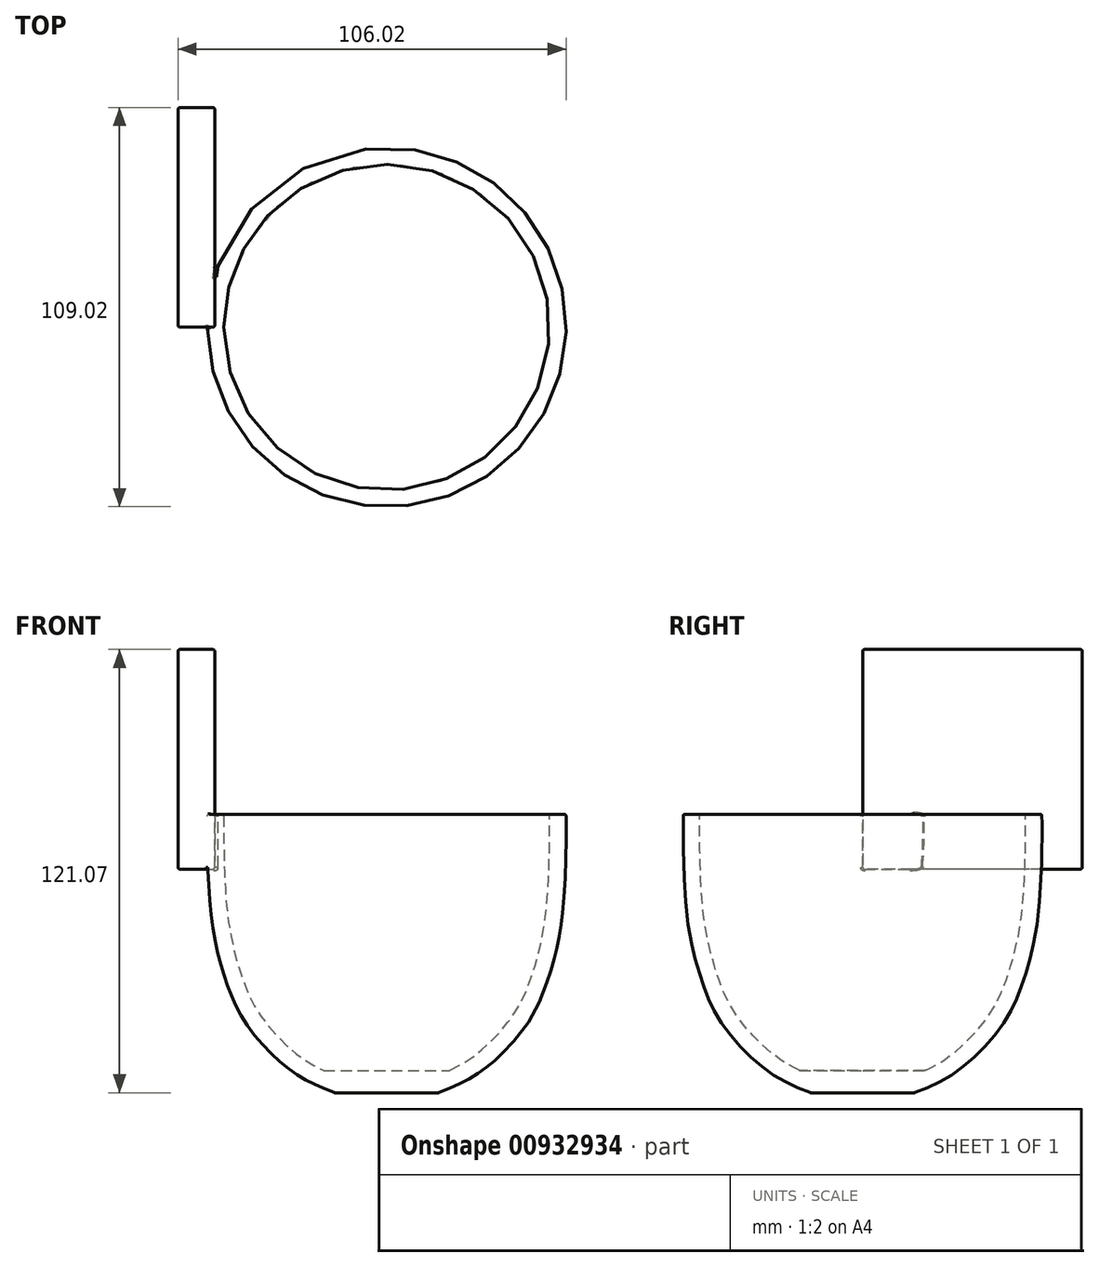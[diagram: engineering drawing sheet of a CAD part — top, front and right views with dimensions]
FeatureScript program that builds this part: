
annotation { "Feature Type Name" : "Feature", "Feature Type Description" : "" }
export const myFeature = defineFeature(function(context is Context, id is Id, definition is map)
    precondition{}
    {
        {
            var Q0;
            Q0=qCreatedBy(makeId("Front.planeOp"),FACE);
            var sketch = newSketch(context, id + "F0", { "sketchPlane" : qUnion([Q0])});
            skLineSegment(sketch, "E0", {"start": v(0, 78.82) * mm, "end": v(-49, 78.82) * mm});
            skLineSegment(sketch, "E1", {"start": v(0, 0) * mm, "end": v(0, 78.82) * mm});
            skFitSpline(sketch, "E2", {"points": [v(-49, 78.82) * mm, v(-49, 71.2) * mm, v(-47.95, 50.94) * mm, v(-44.24, 34.32) * mm, v(-38.54, 21.8) * mm, v(-27.37, 9.77) * mm, v(-17.3, 3.96) * mm, v(0, 0) * mm], "startDerivative": vector(-0.53, -120.05) * mm, "endDerivative": vector(126.32, 0) * mm});
            skSolve(sketch);
        }
        {
            var Q0;
            Q0=qSketchRegion(id+"F0",true);
            var Q1;
            Q1=sQuery(id+"F0.wireOp",EDGE,"E1");
            revolve(context, id + "F1", {"surfaceOperationType" : NewSurfaceOperationType.NEW, "entities" : qUnion([Q0]), "axis" : qUnion([Q1]), "revolveType" : RevolveType.FULL});
        }
        {
            var Q0;
            Q0=makeQuery(id+"F1.opRevolve","SWEPT_FACE",FACE,{"disambiguationData":[OSD([sQuery(id+"F0.wireOp",EDGE,"E0")])]});
            shell(context, id + "F2", {"entities" : qUnion([Q0]), "thickness" : 4.5 * mm});
        }
        {
            var Q0;
            Q0=qCreatedBy(makeId("Front.planeOp"),FACE);
            var sketch = newSketch(context, id + "F3", { "sketchPlane" : qUnion([Q0])});
            skLineSegment(sketch, "E3", {"start": v(-41.77, 30.38) * mm, "end": v(-53.43, 30.38) * mm});
            skLineSegment(sketch, "E4", {"start": v(-49.23, 20.12) * mm, "end": v(-36.53, 20.12) * mm});
            skLineSegment(sketch, "E5", {"start": v(-36.53, 20.12) * mm, "end": v(-41.77, 30.38) * mm});
            skFitSpline(sketch, "E6", {"points": [v(-42.03, 8) * mm, v(-47.44, 16.94) * mm, v(-49.23, 20.12) * mm, v(-51.33, 24.44) * mm, v(-53.43, 30.38) * mm, v(-55.23, 38.72) * mm, v(-56.67, 49.18) * mm, v(-57.32, 61.86) * mm, v(-57.58, 68.13) * mm, v(-57.6, 68.09) * mm], "startDerivative": vector(-47.1, 69.03) * mm, "endDerivative": vector(-6.03, -13.35) * mm});
            skLineSegment(sketch, "E7", {"start": v(-57.58, 68.13) * mm, "end": v(-69.83, 68.13) * mm});
            skFitSpline(sketch, "E8", {"points": [v(-69.83, 68.13) * mm, v(-69.83, 61.07) * mm, v(-69.06, 51.29) * mm, v(-67.63, 40.46) * mm, v(-65.54, 31.18) * mm, v(-63.64, 25) * mm, v(-58.64, 14.66) * mm, v(-54.3, 8) * mm], "startDerivative": vector(-1.12, -53.42) * mm, "endDerivative": vector(31.44, -44.67) * mm});
            skLineSegment(sketch, "E9", {"start": v(-54.3, 8) * mm, "end": v(-42.03, 8) * mm});
            skSolve(sketch);
        }
        {
            var Q0;
            Q0=qCreatedBy(makeId("Right.planeOp"),FACE);
            cPlane(context, id + "F4", {"entities" : qUnion([Q0]), "cplaneType" : CPlaneType.OFFSET, "offset" : 65 * mm, "oppositeDirection" : true, "width" : 150 * mm, "height" : 150 * mm});
        }
        {
            var Q0;
            Q0=qCreatedBy(id+"F4.planeOp",FACE);
            var sketch = newSketch(context, id + "F5", { "sketchPlane" : qUnion([Q0])});
            skPoint(sketch, "E10.middle", {"position": v(0, 24.44) * mm});
            skCircle(sketch, "E11", {"center": v(10, 68.82) * mm, "radius": 6 * mm});
            skSolve(sketch);
        }
        {
            var Q0;
            Q0=qCreatedBy(makeId("Top.planeOp"),FACE);
            cPlane(context, id + "F6", {"entities" : qUnion([Q0]), "cplaneType" : CPlaneType.OFFSET, "offset" : 8 * mm, "width" : 150 * mm, "height" : 150 * mm});
        }
        {
            var Q0;
            Q0=qCreatedBy(makeId("Front.planeOp"),FACE);
            var sketch = newSketch(context, id + "F7", { "sketchPlane" : qUnion([Q0])});
            skLineSegment(sketch, "E12", {"start": v(0, 1.35) * mm, "end": v(0, 8.85) * mm});
            skLineSegment(sketch, "E13", {"start": v(0, 8.85) * mm, "end": v(-21, 8.85) * mm});
            skLineSegment(sketch, "E14", {"start": v(-21, 8.85) * mm, "end": v(0, 1.35) * mm});
            skSolve(sketch);
        }
        {
            var Q0;
            Q0=qSketchRegion(id+"F7",true);
            var Q1;
            Q1=sQuery(id+"F7.wireOp",EDGE,"E12");
            revolve(context, id + "F8", {"operationType" : NewBodyOperationType.ADD, "surfaceOperationType" : NewSurfaceOperationType.NEW, "entities" : qUnion([Q0]), "axis" : qUnion([Q1]), "revolveType" : RevolveType.FULL});
        }
        {
            var Q0;
            Q0=qCreatedBy(makeId("Front.planeOp"),FACE);
            var sketch = newSketch(context, id + "F9", { "sketchPlane" : qUnion([Q0])});
            skLineSegment(sketch, "E15.bottom", {"start": v(20, 0) * mm, "end": v(-20, 0) * mm});
            skLineSegment(sketch, "E15.top", {"start": v(20, 2.75) * mm, "end": v(-20, 2.75) * mm});
            skLineSegment(sketch, "E15.left", {"start": v(20, 0) * mm, "end": v(20, 2.75) * mm});
            skLineSegment(sketch, "E15.right", {"start": v(-20, 0) * mm, "end": v(-20, 2.75) * mm});
            skSolve(sketch);
        }
        {
            var Q0;
            Q0=qSketchRegion(id+"F9",true);
            extrude(context, id + "F10", {"entities" : qUnion([Q0]), "operationType" : NewBodyOperationType.REMOVE, "oppositeDirection" : true, "depth" : 40 * mm, "offsetDistance" : 25 * mm, "symmetric" : true});
        }
        {
            var Q0;
            Q0=qCreatedBy(makeId("Front.planeOp"),FACE);
            var sketch = newSketch(context, id + "F11", { "sketchPlane" : qUnion([Q0])});
            skLineSegment(sketch, "E16", {"start": v(-47, 123.82) * mm, "end": v(-57, 123.82) * mm});
            skLineSegment(sketch, "E17", {"start": v(-57, 123.82) * mm, "end": v(-57, 63.82) * mm});
            skLineSegment(sketch, "E18", {"start": v(-57, 63.82) * mm, "end": v(-47, 63.82) * mm});
            skLineSegment(sketch, "E19", {"start": v(-47, 63.82) * mm, "end": v(-47, 123.82) * mm});
            skSolve(sketch);
        }
        {
            var Q0;
            Q0=makeQuery(id+"F11.imprint","IMPRINT",FACE,{"disambiguationData":[TD([[makeQuery(id+"F11.imprint","IMPRINT",EDGE,{"derivedFrom":sQuery(id+"F11.wireOp",EDGE,"E16")}),1.0]])]});
            extrude(context, id + "F12", {"entities" : qUnion([Q0]), "operationType" : NewBodyOperationType.ADD, "oppositeDirection" : true, "depth" : 60 * mm, "offsetDistance" : 25 * mm});
        }
        {
            var Q0;
            Q0=makeQuery(id+"F1.opRevolve","SWEPT_FACE",FACE,{"disambiguationData":[OSD([sQuery(id+"F0.wireOp",EDGE,"E0")])]});
            var Q1;
            Q1=makeQuery(id+"F8.opRevolve","SWEPT_FACE",FACE,{"disambiguationData":[OSD([sQuery(id+"F7.wireOp",EDGE,"E13")])]});
            var Q2;
            Q2=makeQuery(id+"F10.boolean.opBoolean","COPY",FACE,{"derivedFrom":makeQuery(id+"F10.opExtrude","SWEPT_FACE",FACE,{"disambiguationData":[OSD([sQuery(id+"F9.wireOp",EDGE,"E15.top")])]})});
            var Q3;
            Q3=makeQuery(id+"F12.opExtrude","SWEPT_FACE",FACE,{"disambiguationData":[OSD([sQuery(id+"F11.wireOp",EDGE,"E19")])]});
            var Q4;
            Q4=makeQuery(id+"F12.opExtrude","SWEPT_FACE",FACE,{"disambiguationData":[OSD([sQuery(id+"F11.wireOp",EDGE,"E16")])]});
            var Q5;
            Q5=makeQuery(id+"F12.opExtrude","SWEPT_FACE",FACE,{"disambiguationData":[OSD([sQuery(id+"F11.wireOp",EDGE,"E17")])]});
            var Q6;
            Q6=makeQuery(id+"F12.opExtrude","SWEPT_FACE",FACE,{"disambiguationData":[OSD([sQuery(id+"F11.wireOp",EDGE,"E18")])]});
            var Q7;
            Q7=makeQuery(id+"F12.opExtrude","CAP_FACE",FACE,{"disambiguationData":[OSD([sQuery(id+"F11.wireOp",EDGE,"E16"),sQuery(id+"F11.wireOp",EDGE,"E17"),sQuery(id+"F11.wireOp",EDGE,"E18"),sQuery(id+"F11.wireOp",EDGE,"E19")])],"isStart":true});
            var Q8;
            Q8=makeQuery(id+"F12.opExtrude","CAP_FACE",FACE,{"disambiguationData":[OSD([sQuery(id+"F11.wireOp",EDGE,"E16"),sQuery(id+"F11.wireOp",EDGE,"E17"),sQuery(id+"F11.wireOp",EDGE,"E18"),sQuery(id+"F11.wireOp",EDGE,"E19")])],"isStart":false});
            fillet(context, id + "F13", {"entities" : qUnion([Q0, Q1, Q2, Q3, Q4, Q5, Q6, Q7, Q8]), "tangentPropagation" : true, "radius" : .5 * mm, "defaultsChanged" : false, "vertexSettings" : [], "allowEdgeOverflow" : false});
        }
    });
